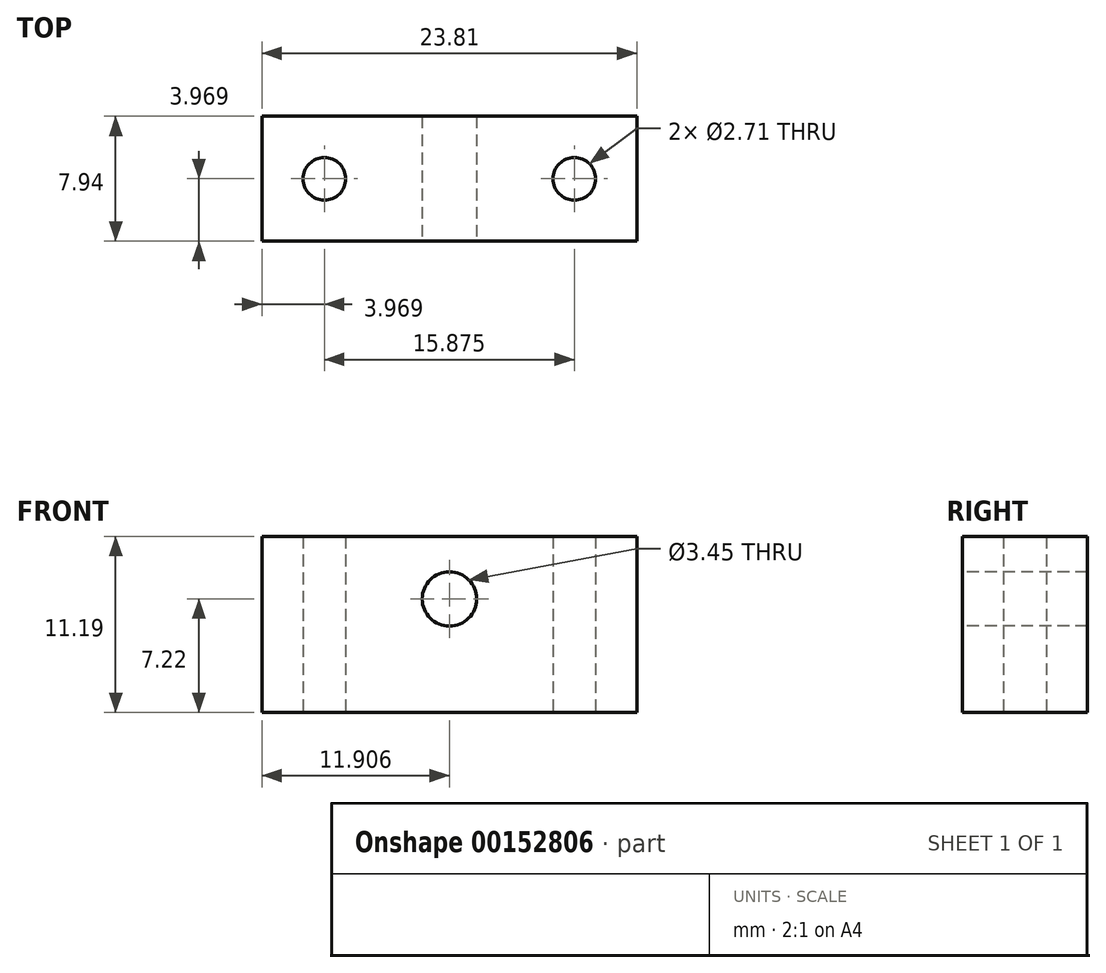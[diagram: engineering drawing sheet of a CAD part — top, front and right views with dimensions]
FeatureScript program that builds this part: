
annotation { "Feature Type Name" : "Feature", "Feature Type Description" : "" }
export const myFeature = defineFeature(function(context is Context, id is Id, definition is map)
    precondition{}
    {
        {
            var Q0;
            Q0=qCreatedBy(makeId("Top.planeOp"),FACE);
            var sketch = newSketch(context, id + "F0", { "sketchPlane" : qUnion([Q0])});
            skLineSegment(sketch, "E0.bottom", {"start": v(0, 0) * mm, "end": v(23.81, 0) * mm});
            skLineSegment(sketch, "E0.top", {"start": v(0, 7.94) * mm, "end": v(23.81, 7.94) * mm});
            skLineSegment(sketch, "E0.left", {"start": v(0, 0) * mm, "end": v(0, 7.94) * mm});
            skLineSegment(sketch, "E0.right", {"start": v(23.81, 0) * mm, "end": v(23.81, 7.94) * mm});
            skLineSegment(sketch, "E1", {"start": v(0, 3.97) * mm, "end": v(3.97, 3.97) * mm, "construction": true});
            skLineSegment(sketch, "E2", {"start": v(23.81, 3.97) * mm, "end": v(19.84, 3.97) * mm, "construction": true});
            skLineSegment(sketch, "E3", {"start": v(3.97, 3.97) * mm, "end": v(3.97, 7.94) * mm, "construction": true});
            skCircle(sketch, "E4", {"center": v(3.97, 3.97) * mm, "radius": 1.35 * mm});
            skCircle(sketch, "E5", {"center": v(19.84, 3.97) * mm, "radius": 1.35 * mm});
            skSolve(sketch);
        }
        {
            var Q0;
            Q0 = qSketchRegion(id + "F0", true);
            extrude(context, id + "F1", {"entities" : qUnion([Q0]), "depth" : 11.2 * mm});
        }
        {
            var Q0;
            Q0=makeQuery(id+"F1.opExtrude","SWEPT_FACE",FACE,{"disambiguationData":[OSD([sQuery(id+"F0.wireOp",EDGE,"E0.bottom")])]});
            var sketch = newSketch(context, id + "F2", { "sketchPlane" : qUnion([Q0])});
            skLineSegment(sketch, "E6", {"start": v(11.9, 0) * mm, "end": v(11.9, 7.22) * mm, "construction": true});
            skCircle(sketch, "E7", {"center": v(11.9, 7.22) * mm, "radius": 1.73 * mm});
            skSolve(sketch);
        }
        {
            var Q0;
            Q0 = qSketchRegion(id + "F2", true);
            var Q1;
            Q1=makeQuery(id+"F1.opExtrude","SWEPT_FACE",FACE,{"disambiguationData":[OSD([sQuery(id+"F0.wireOp",EDGE,"E0.top")])]});
            extrude(context, id + "F3", {"entities" : qUnion([Q0]), "operationType" : NewBodyOperationType.REMOVE, "endBound" : BoundingType.UP_TO_SURFACE, "oppositeDirection" : true, "endBoundEntityFace" : qUnion([Q1]), "depth" : 25.4 * mm});
        }
    });
